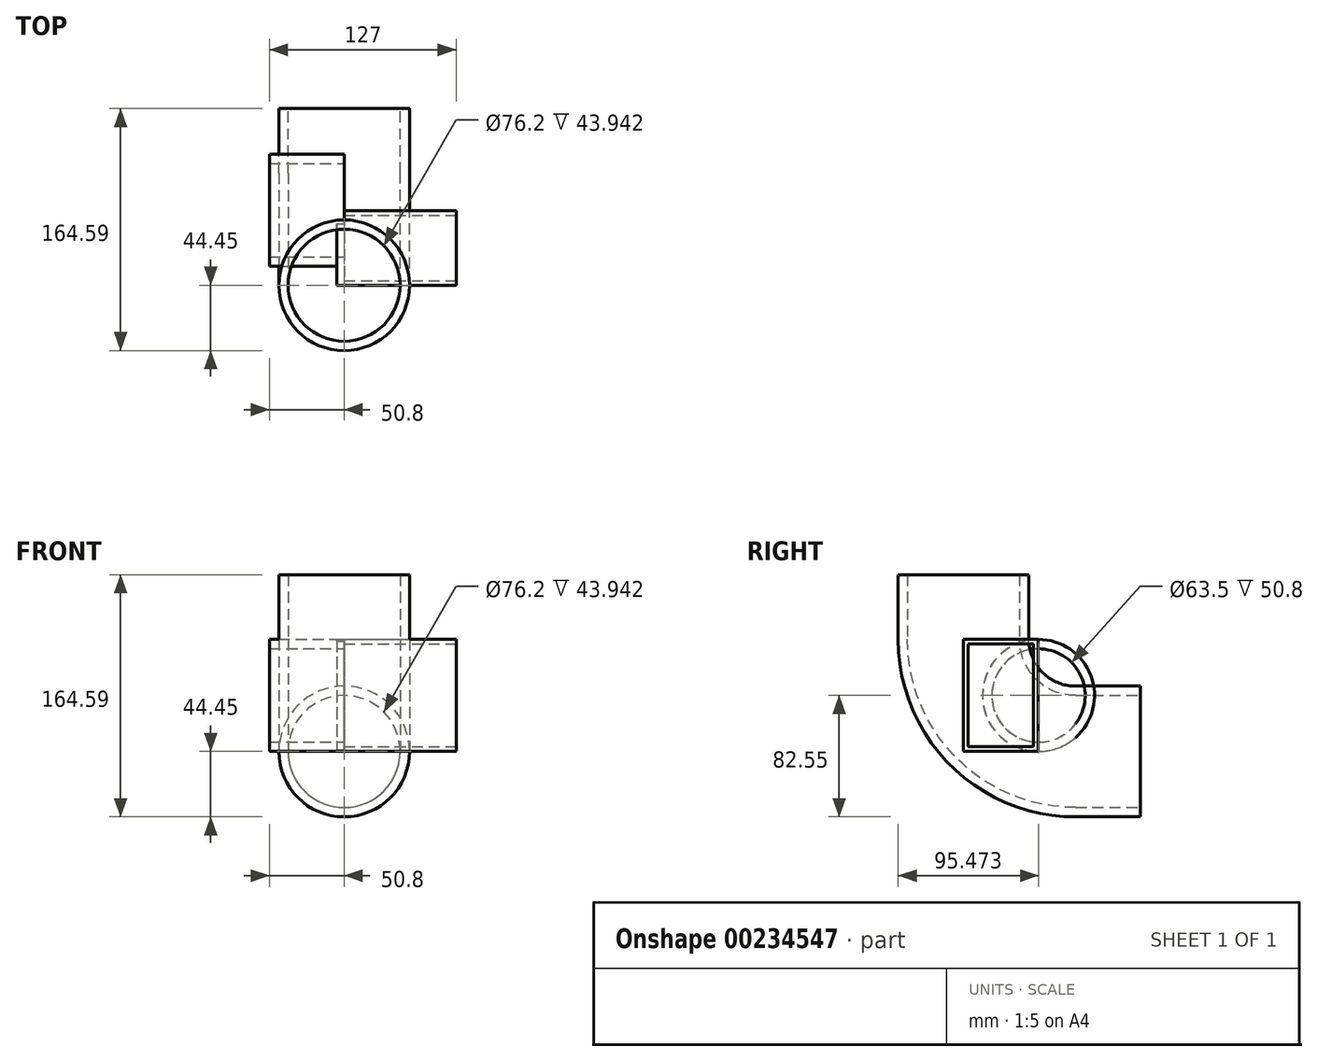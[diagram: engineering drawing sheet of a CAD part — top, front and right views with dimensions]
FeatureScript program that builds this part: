
annotation { "Feature Type Name" : "Feature", "Feature Type Description" : "" }
export const myFeature = defineFeature(function(context is Context, id is Id, definition is map)
    precondition{}
    {
        {
            var Q0;
            Q0=qCreatedBy(makeId("Top.planeOp"),FACE);
            var sketch = newSketch(context, id + "F0", { "sketchPlane" : qUnion([Q0])});
            skLineSegment(sketch, "E0.bottom", {"start": v(0, 0) * mm, "end": v(76.2, 0) * mm});
            skLineSegment(sketch, "E0.top", {"start": v(0, 50.8) * mm, "end": v(76.2, 50.8) * mm});
            skLineSegment(sketch, "E0.left", {"start": v(0, 0) * mm, "end": v(0, 50.8) * mm});
            skLineSegment(sketch, "E0.right", {"start": v(76.2, 0) * mm, "end": v(76.2, 50.8) * mm});
            skSolve(sketch);
        }
        {
            var Q0;
            Q0 = qSketchRegion(id + "F0", true);
            extrude(context, id + "F1", {"entities" : qUnion([Q0]), "depth" : 76.2 * mm});
        }
        {
            var Q0;
            Q0=makeQuery(id+"F1.opExtrude","SWEPT_FACE",FACE,{"disambiguationData":[OSD([sQuery(id+"F0.wireOp",EDGE,"E0.right")])]});
            var sketch = newSketch(context, id + "F2", { "sketchPlane" : qUnion([Q0])});
            skLineSegment(sketch, "E1.bottom", {"start": v(47.62, 73.03) * mm, "end": v(3.17, 73.03) * mm});
            skLineSegment(sketch, "E1.top", {"start": v(47.63, 3.18) * mm, "end": v(3.18, 3.17) * mm});
            skLineSegment(sketch, "E1.left", {"start": v(47.62, 73.03) * mm, "end": v(47.63, 3.18) * mm});
            skLineSegment(sketch, "E1.right", {"start": v(3.17, 73.03) * mm, "end": v(3.18, 3.17) * mm});
            skSolve(sketch);
        }
        {
            var Q0;
            Q0 = qSketchRegion(id + "F2", true);
            extrude(context, id + "F3", {"entities" : qUnion([Q0]), "operationType" : NewBodyOperationType.REMOVE, "endBound" : BoundingType.UP_TO_NEXT, "oppositeDirection" : true, "depth" : 25.4 * mm});
        }
        {
            var Q0;
            Q0=qCreatedBy(makeId("Right.planeOp"),FACE);
            var sketch = newSketch(context, id + "F4", { "sketchPlane" : qUnion([Q0])});
            skCircle(sketch, "E2", {"center": v(51.02, 38.1) * mm, "radius": 38.1 * mm});
            skCircle(sketch, "E3", {"center": v(51.02, 38.1) * mm, "radius": 31.75 * mm});
            skSolve(sketch);
        }
        {
            var Q0;
            Q0=makeQuery(id+"F4.imprint","IMPRINT",FACE,{"disambiguationData":[TD([[makeQuery(id+"F4.imprint","IMPRINT",EDGE,{"derivedFrom":sQuery(id+"F4.wireOp",EDGE,"E2")}),1.0]])]});
            extrude(context, id + "F5", {"entities" : qUnion([Q0]), "operationType" : NewBodyOperationType.ADD, "oppositeDirection" : true, "depth" : 50.8 * mm});
        }
        {
            var Q0;
            Q0=qCreatedBy(makeId("Right.planeOp"),FACE);
            var sketch = newSketch(context, id + "F6", { "sketchPlane" : qUnion([Q0])});
            skArc(sketch, "E4.0", {"start": v(41.9, 75.1) * mm, "mid": v(12.92, 38.1) * mm, "end": v(41.91, 1.1) * mm});
            skLineSegment(sketch, "E4.1", {"start": v(0, 76.2) * mm, "end": v(41.9, 76.2) * mm});
            skLineSegment(sketch, "E4.2", {"start": v(0, 76.2) * mm, "end": v(0, 0) * mm});
            skLineSegment(sketch, "E4.3", {"start": v(0, 0) * mm, "end": v(41.9, 0) * mm});
            skLineSegment(sketch, "E5", {"start": v(41.9, 75.1) * mm, "end": v(41.9, 76.2) * mm});
            skLineSegment(sketch, "E6", {"start": v(51.02, 38.1) * mm, "end": v(150.43, 38.1) * mm, "construction": true});
            skLineSegment(sketch, "E7", {"start": v(41.9, 0) * mm, "end": v(41.9, 1.1) * mm});
            skPoint(sketch, "E8.orphan", {"position": v(50.8, 76.2) * mm});
            skPoint(sketch, "E9.orphan", {"position": v(50.8, 0) * mm});
            skSolve(sketch);
        }
        {
            var Q0;
            Q0 = qSketchRegion(id + "F6", true);
            extrude(context, id + "F7", {"entities" : qUnion([Q0]), "operationType" : NewBodyOperationType.ADD, "oppositeDirection" : true, "depth" : 5.08 * mm});
        }
        {
            var Q0;
            Q0=qCreatedBy(makeId("Right.planeOp"),FACE);
            var sketch = newSketch(context, id + "F8", { "sketchPlane" : qUnion([Q0])});
            skLineSegment(sketch, "E10", {"start": v(0, 120.14) * mm, "end": v(0, 76.2) * mm});
            skLineSegment(sketch, "E11", {"start": v(76.2, 0) * mm, "end": v(120.14, 0) * mm});
            skPoint(sketch, "E12.visualSharp", {"position": v(0, 0) * mm});
            skArc(sketch, "E12.filletArc", {"start": v(0, 76.2) * mm, "mid": v(22.32, 22.32) * mm, "end": v(76.2, 0) * mm});
            skSolve(sketch);
        }
        {
            var Q0;
            Q0=qCreatedBy(makeId("Top.planeOp"),FACE);
            var Q1;
            Q1=sQuery(id+"F8.wireOp",VERTEX,"E10.start");
            cPlane(context, id + "F9", {"entities" : qUnion([Q0, Q1]), "cplaneType" : CPlaneType.PLANE_POINT, "offset" : 25.4 * mm, "width" : 152.4 * mm, "height" : 152.4 * mm});
        }
        {
            var Q0;
            Q0=qCreatedBy(id+"F9.planeOp",FACE);
            var sketch = newSketch(context, id + "F10", { "sketchPlane" : qUnion([Q0])});
            skCircle(sketch, "E13", {"center": v(0, 0) * mm, "radius": 44.45 * mm});
            skCircle(sketch, "E14", {"center": v(0, 0) * mm, "radius": 38.1 * mm});
            skSolve(sketch);
        }
        {
            var Q0;
            Q0 = qSketchRegion(id + "F10", true);
            var Q1;
            Q1 = qConstructionFilter(qBodyType(qCreatedBy(id + "F8" ,EDGE), BodyType.WIRE), ConstructionObject.NO);
            sweep(context, id + "F11", {"profiles" : qUnion([Q0]), "path" : qUnion([Q1])});
        }
    });
